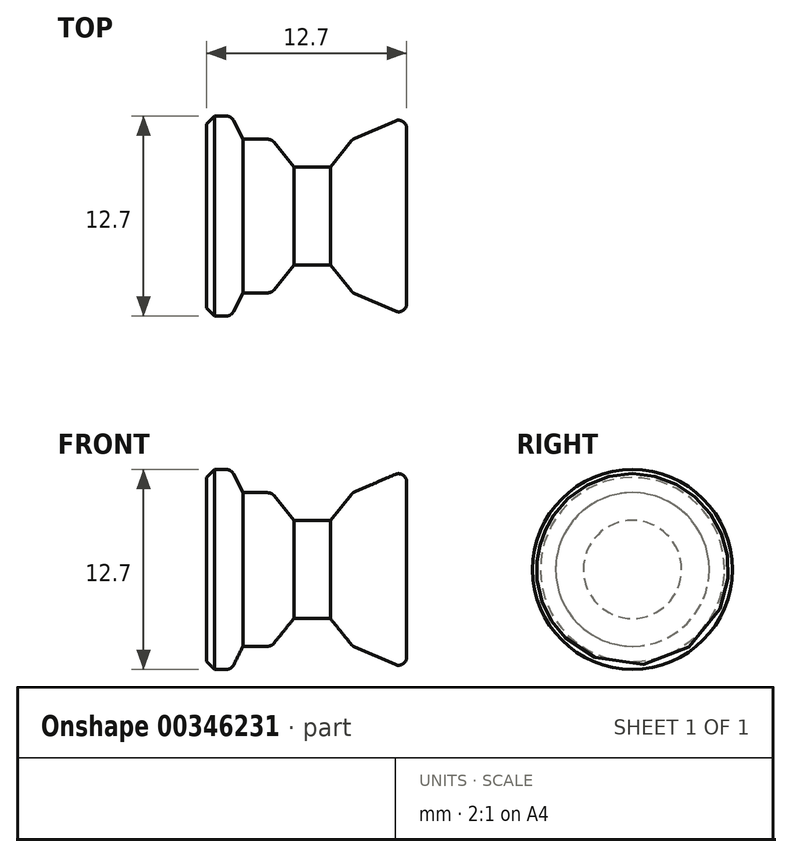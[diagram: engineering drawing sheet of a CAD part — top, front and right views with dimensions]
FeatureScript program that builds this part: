
annotation { "Feature Type Name" : "Feature", "Feature Type Description" : "" }
export const myFeature = defineFeature(function(context is Context, id is Id, definition is map)
    precondition{}
    {
        {
            var Q0;
            Q0=qCreatedBy(makeId("Front.planeOp"),FACE);
            var sketch = newSketch(context, id + "F0", { "sketchPlane" : qUnion([Q0])});
            skLineSegment(sketch, "E0", {"start": v(0, 0) * mm, "end": v(-12.7, 0) * mm});
            skLineSegment(sketch, "E1", {"start": v(-12.7, 0) * mm, "end": v(-12.7, 6.35) * mm});
            skLineSegment(sketch, "E2", {"start": v(-12.7, 6.35) * mm, "end": v(-11.13, 6.35) * mm});
            skLineSegment(sketch, "E3", {"start": v(-11.13, 6.35) * mm, "end": v(-10.39, 4.88) * mm});
            skLineSegment(sketch, "E4", {"start": v(-10.39, 4.88) * mm, "end": v(-8.57, 4.88) * mm});
            skLineSegment(sketch, "E5", {"start": v(-8.57, 4.88) * mm, "end": v(-7.16, 3.12) * mm});
            skLineSegment(sketch, "E6", {"start": v(-7.16, 3.12) * mm, "end": v(-4.83, 3.12) * mm});
            skLineSegment(sketch, "E7", {"start": v(-4.83, 3.12) * mm, "end": v(-3.42, 4.88) * mm});
            skLineSegment(sketch, "E8", {"start": v(-3.42, 4.88) * mm, "end": v(0, 6.35) * mm});
            skLineSegment(sketch, "E9", {"start": v(0, 6.35) * mm, "end": v(0, 0) * mm});
            skSolve(sketch);
        }
        {
            var Q0;
            Q0=makeQuery(id+"F0.imprint","IMPRINT",FACE,{"disambiguationData":[TD([[makeQuery(id+"F0.imprint","IMPRINT",EDGE,{"derivedFrom":sQuery(id+"F0.wireOp",EDGE,"E0")}),-1.0]])]});
            var Q1;
            Q1=sQuery(id+"F0.wireOp",EDGE,"E0");
            revolve(context, id + "F1", {"entities" : qUnion([Q0]), "axis" : qUnion([Q1]), "revolveType" : RevolveType.FULL});
        }
        {
            var Q0;
            Q0=makeQuery(id+"F1.opRevolve","SWEPT_FACE",FACE,{"disambiguationData":[OSD([sQuery(id+"F0.wireOp",EDGE,"E9")])]});
            var Q1;
            Q1=makeQuery(id+"F1.opRevolve","SWEPT_EDGE",EDGE,{"disambiguationData":[OSD([sQuery(id+"F0.wireOp",EDGE,"E7"),sQuery(id+"F0.wireOp",EDGE,"E8")])]});
            var Q2;
            Q2=makeQuery(id+"F1.opRevolve","SWEPT_EDGE",EDGE,{"disambiguationData":[OSD([sQuery(id+"F0.wireOp",EDGE,"E4"),sQuery(id+"F0.wireOp",EDGE,"E5")])]});
            var Q3;
            Q3=makeQuery(id+"F1.opRevolve","SWEPT_EDGE",EDGE,{"disambiguationData":[OSD([sQuery(id+"F0.wireOp",EDGE,"E2"),sQuery(id+"F0.wireOp",EDGE,"E3")])]});
            fillet(context, id + "F2", {"entities" : qUnion([Q0, Q1, Q2, Q3]), "radius" : 0.5 * mm, "tangentPropagation" : true, "allowEdgeOverflow" : false});
        }
        {
            var Q0;
            Q0=makeQuery(id+"F1.opRevolve","SWEPT_EDGE",EDGE,{"disambiguationData":[OSD([sQuery(id+"F0.wireOp",EDGE,"E1"),sQuery(id+"F0.wireOp",EDGE,"E2")])]});
            chamfer(context, id + "F3", {"entities" : qUnion([Q0]), "width" : 0.5 * mm, "tangentPropagation" : true});
        }
    });
